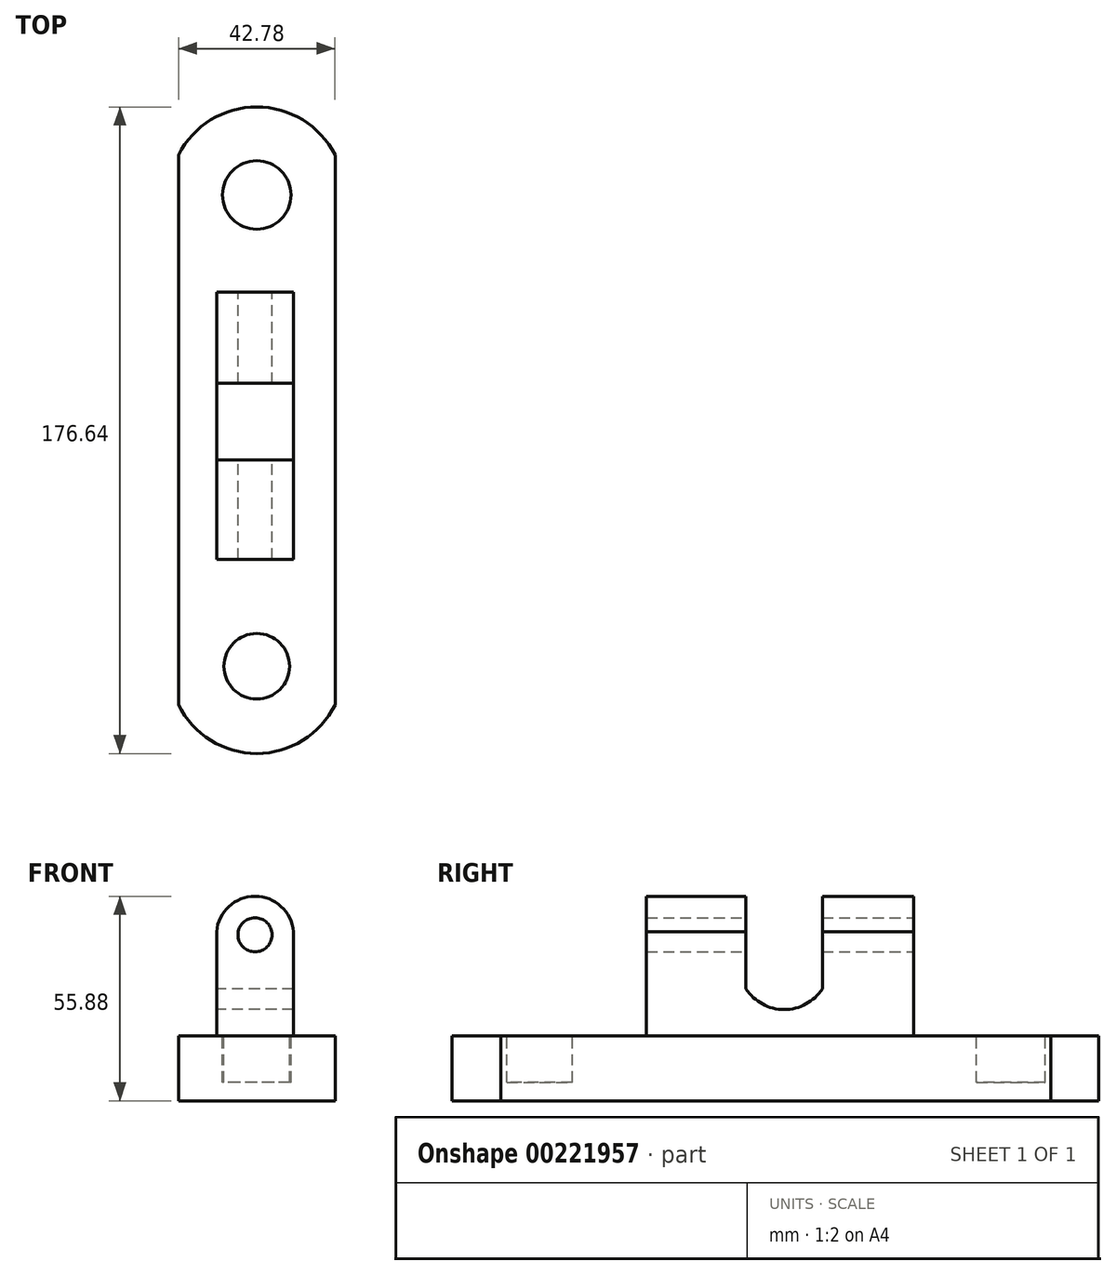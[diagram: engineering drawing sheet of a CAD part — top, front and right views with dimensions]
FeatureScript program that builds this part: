
annotation { "Feature Type Name" : "Feature", "Feature Type Description" : "" }
export const myFeature = defineFeature(function(context is Context, id is Id, definition is map)
    precondition{}
    {
        {
            var Q0;
            Q0=qCreatedBy(makeId("Top.planeOp"),FACE);
            var sketch = newSketch(context, id + "F0", { "sketchPlane" : qUnion([Q0])});
            skLineSegment(sketch, "E0", {"start": v(24.18, -76) * mm, "end": v(24.18, 74.26) * mm});
            skLineSegment(sketch, "E1", {"start": v(24.18, 74.26) * mm, "end": v(24.18, -76) * mm});
            skLineSegment(sketch, "E2", {"start": v(-18.6, -76) * mm, "end": v(-18.6, 74.26) * mm});
            skLineSegment(sketch, "E3", {"start": v(-18.6, 74.26) * mm, "end": v(-18.6, -76) * mm});
            skArc(sketch, "E4", {"start": v(24.18, 74.26) * mm, "mid": v(2.79, 87.32) * mm, "end": v(-18.6, 74.26) * mm});
            skArc(sketch, "E5", {"start": v(-18.6, -76) * mm, "mid": v(2.79, -89.32) * mm, "end": v(24.18, -76) * mm});
            skSolve(sketch);
        }
        {
            var Q0;
            Q0 = qSketchRegion(id + "F0", true);
            extrude(context, id + "F1", {"entities" : qUnion([Q0]), "depth" : 17.78 * mm});
        }
        {
            var Q0;
            Q0=makeQuery(id+"F1.opExtrude","CAP_FACE",FACE,{"disambiguationData":[OSD([sQuery(id+"F0.wireOp",EDGE,"E1"),sQuery(id+"F0.wireOp",EDGE,"E3"),sQuery(id+"F0.wireOp",EDGE,"E4"),sQuery(id+"F0.wireOp",EDGE,"E5")])],"isStart":false});
            var sketch = newSketch(context, id + "F2", { "sketchPlane" : qUnion([Q0])});
            skCircle(sketch, "E6", {"center": v(2.79, -65.5) * mm, "radius": 8.96 * mm});
            skCircle(sketch, "E7", {"center": v(2.79, 63.28) * mm, "radius": 9.36 * mm});
            skSolve(sketch);
        }
        {
            var Q0;
            Q0 = qSketchRegion(id + "F2", true);
            extrude(context, id + "F3", {"entities" : qUnion([Q0]), "operationType" : NewBodyOperationType.REMOVE, "oppositeDirection" : true, "depth" : 12.7 * mm});
        }
        {
            var Q0;
            Q0=makeQuery(id+"F1.opExtrude","CAP_FACE",FACE,{"disambiguationData":[OSD([sQuery(id+"F0.wireOp",EDGE,"E1"),sQuery(id+"F0.wireOp",EDGE,"E3"),sQuery(id+"F0.wireOp",EDGE,"E4"),sQuery(id+"F0.wireOp",EDGE,"E5")])],"isStart":false});
            var sketch = newSketch(context, id + "F4", { "sketchPlane" : qUnion([Q0])});
            skLineSegment(sketch, "E8", {"start": v(12.81, -36.24) * mm, "end": v(12.81, 36.74) * mm});
            skLineSegment(sketch, "E9", {"start": v(-8.19, 36.74) * mm, "end": v(-8.19, -36.24) * mm});
            skLineSegment(sketch, "E10", {"start": v(12.81, -36.24) * mm, "end": v(-8.19, -36.24) * mm});
            skLineSegment(sketch, "E11", {"start": v(-8.19, 36.74) * mm, "end": v(12.81, 36.74) * mm});
            skSolve(sketch);
        }
        {
            var Q0;
            Q0 = qSketchRegion(id + "F4", true);
            extrude(context, id + "F5", {"entities" : qUnion([Q0]), "operationType" : NewBodyOperationType.ADD, "depth" : 38.1 * mm});
        }
        {
            var Q0;
            Q0=makeQuery(id+"F5.opExtrude","SWEPT_FACE",FACE,{"disambiguationData":[OSD([sQuery(id+"F4.wireOp",EDGE,"E11")])]});
            var sketch = newSketch(context, id + "F6", { "sketchPlane" : qUnion([Q0])});
            skLineSegment(sketch, "E12", {"start": v(-12.81, 46.22) * mm, "end": v(-12.81, 55.88) * mm});
            skLineSegment(sketch, "E13", {"start": v(-12.81, 55.88) * mm, "end": v(-2.31, 55.88) * mm});
            skLineSegment(sketch, "E14", {"start": v(-2.31, 55.88) * mm, "end": v(-12.81, 55.88) * mm});
            skArc(sketch, "E15", {"start": v(-2.31, 55.88) * mm, "mid": v(-9.45, 53.1) * mm, "end": v(-12.81, 46.22) * mm});
            skArc(sketch, "E16", {"start": v(8.19, 46.22) * mm, "mid": v(4.82, 53.1) * mm, "end": v(-2.31, 55.88) * mm});
            skLineSegment(sketch, "E17", {"start": v(8.19, 46.22) * mm, "end": v(8.19, 55.88) * mm});
            skLineSegment(sketch, "E18", {"start": v(8.19, 55.88) * mm, "end": v(-2.31, 55.88) * mm});
            skSolve(sketch);
        }
        {
            var Q0;
            Q0 = qSketchRegion(id + "F6", true);
            extrude(context, id + "F7", {"entities" : qUnion([Q0]), "operationType" : NewBodyOperationType.REMOVE, "endBound" : BoundingType.THROUGH_ALL, "oppositeDirection" : true, "depth" : 25.4 * mm});
        }
        {
            var Q0;
            Q0=makeQuery(id+"F5.opExtrude","SWEPT_FACE",FACE,{"disambiguationData":[OSD([sQuery(id+"F4.wireOp",EDGE,"E9")])]});
            var sketch = newSketch(context, id + "F8", { "sketchPlane" : qUnion([Q0])});
            skLineSegment(sketch, "E19", {"start": v(-11.8, 56.16) * mm, "end": v(-11.8, 30.56) * mm});
            skLineSegment(sketch, "E20", {"start": v(-11.8, 30.56) * mm, "end": v(-11.8, 56.16) * mm});
            skLineSegment(sketch, "E21", {"start": v(9.08, 56.16) * mm, "end": v(9.08, 30.56) * mm});
            skLineSegment(sketch, "E22", {"start": v(9.08, 30.56) * mm, "end": v(9.08, 56.16) * mm});
            skArc(sketch, "E23", {"start": v(-11.8, 30.56) * mm, "mid": v(-1.36, 24.93) * mm, "end": v(9.08, 30.56) * mm});
            skLineSegment(sketch, "E24", {"start": v(9.08, 56.16) * mm, "end": v(-11.8, 56.16) * mm});
            skSolve(sketch);
        }
        {
            var Q0;
            Q0 = qSketchRegion(id + "F8", true);
            extrude(context, id + "F9", {"entities" : qUnion([Q0]), "operationType" : NewBodyOperationType.REMOVE, "endBound" : BoundingType.THROUGH_ALL, "oppositeDirection" : true, "depth" : 25.4 * mm});
        }
        {
            var Q0;
            Q0=makeQuery(id+"F5.opExtrude","SWEPT_FACE",FACE,{"disambiguationData":[OSD([sQuery(id+"F4.wireOp",EDGE,"E11")])]});
            var sketch = newSketch(context, id + "F10", { "sketchPlane" : qUnion([Q0])});
            skCircle(sketch, "E25", {"center": v(-2.31, 45.34) * mm, "radius": 4.65 * mm});
            skSolve(sketch);
        }
        {
            var Q0;
            Q0 = qSketchRegion(id + "F10", true);
            extrude(context, id + "F11", {"entities" : qUnion([Q0]), "operationType" : NewBodyOperationType.REMOVE, "endBound" : BoundingType.THROUGH_ALL, "oppositeDirection" : true, "depth" : 25.4 * mm});
        }
    });
